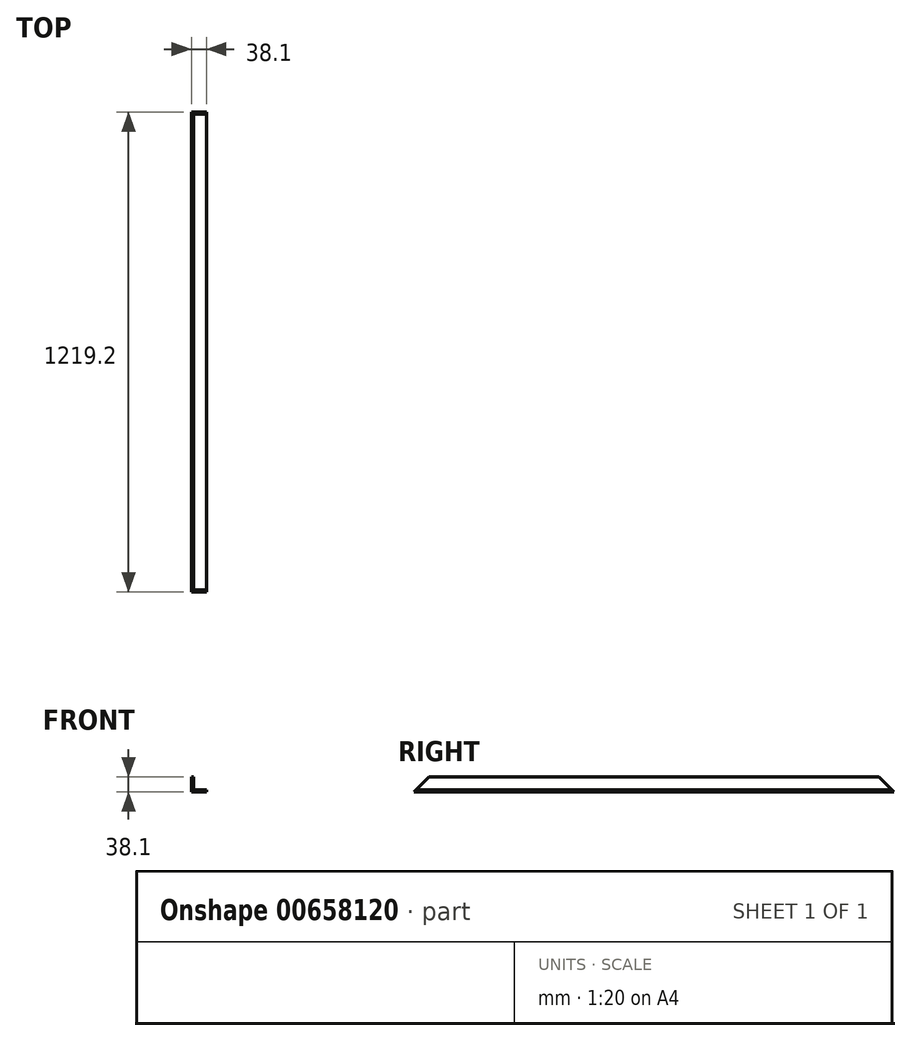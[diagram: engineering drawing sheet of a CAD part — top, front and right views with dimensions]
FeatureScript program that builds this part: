
annotation { "Feature Type Name" : "Feature", "Feature Type Description" : "" }
export const myFeature = defineFeature(function(context is Context, id is Id, definition is map)
    precondition{}
    {
        {
            var Q0;
            Q0=qCreatedBy(makeId("Front.planeOp"),FACE);
            var sketch = newSketch(context, id + "F0", { "sketchPlane" : qUnion([Q0])});
            skLineSegment(sketch, "E0", {"start": v(0, 0) * mm, "end": v(0, 38.1) * mm});
            skLineSegment(sketch, "E1", {"start": v(0, 38.1) * mm, "end": v(4.76, 38.1) * mm});
            skLineSegment(sketch, "E2", {"start": v(4.76, 38.1) * mm, "end": v(4.76, 4.76) * mm});
            skLineSegment(sketch, "E3", {"start": v(4.76, 4.76) * mm, "end": v(38.1, 4.76) * mm});
            skLineSegment(sketch, "E4", {"start": v(38.1, 4.76) * mm, "end": v(38.1, 0) * mm});
            skLineSegment(sketch, "E5", {"start": v(38.1, 0) * mm, "end": v(0, 0) * mm});
            skSolve(sketch);
        }
        {
            var Q0;
            Q0=qSketchRegion(id+"F0",true);
            extrude(context, id + "F1", {"entities" : qUnion([Q0]), "depth" : 1219.2 * mm, "offsetDistance" : 25.4 * mm});
        }
        {
            var Q0;
            Q0=makeQuery(id+"F1.opExtrude","SWEPT_FACE",FACE,{"disambiguationData":[OSD([sQuery(id+"F0.wireOp",EDGE,"E0")])]});
            var sketch = newSketch(context, id + "F2", { "sketchPlane" : qUnion([Q0])});
            skLineSegment(sketch, "E6.0", {"start": v(1219.2, 0) * mm, "end": v(1219.2, 38.1) * mm});
            skLineSegment(sketch, "E6.1", {"start": v(1219.2, 38.1) * mm, "end": v(0, 38.1) * mm});
            skLineSegment(sketch, "E6.2", {"start": v(0, 0) * mm, "end": v(0, 38.1) * mm});
            skLineSegment(sketch, "E7", {"start": v(0, 0) * mm, "end": v(38.1, 38.1) * mm});
            skLineSegment(sketch, "E8", {"start": v(1219.2, 0) * mm, "end": v(1181.1, 38.1) * mm});
            skSolve(sketch);
        }
        {
            var Q0;
            Q0=qSketchRegion(id+"F2",true);
            extrude(context, id + "F3", {"entities" : qUnion([Q0]), "operationType" : NewBodyOperationType.REMOVE, "endBound" : BoundingType.THROUGH_ALL, "oppositeDirection" : true, "depth" : 25.4 * mm, "offsetDistance" : 25.4 * mm});
        }
    });
